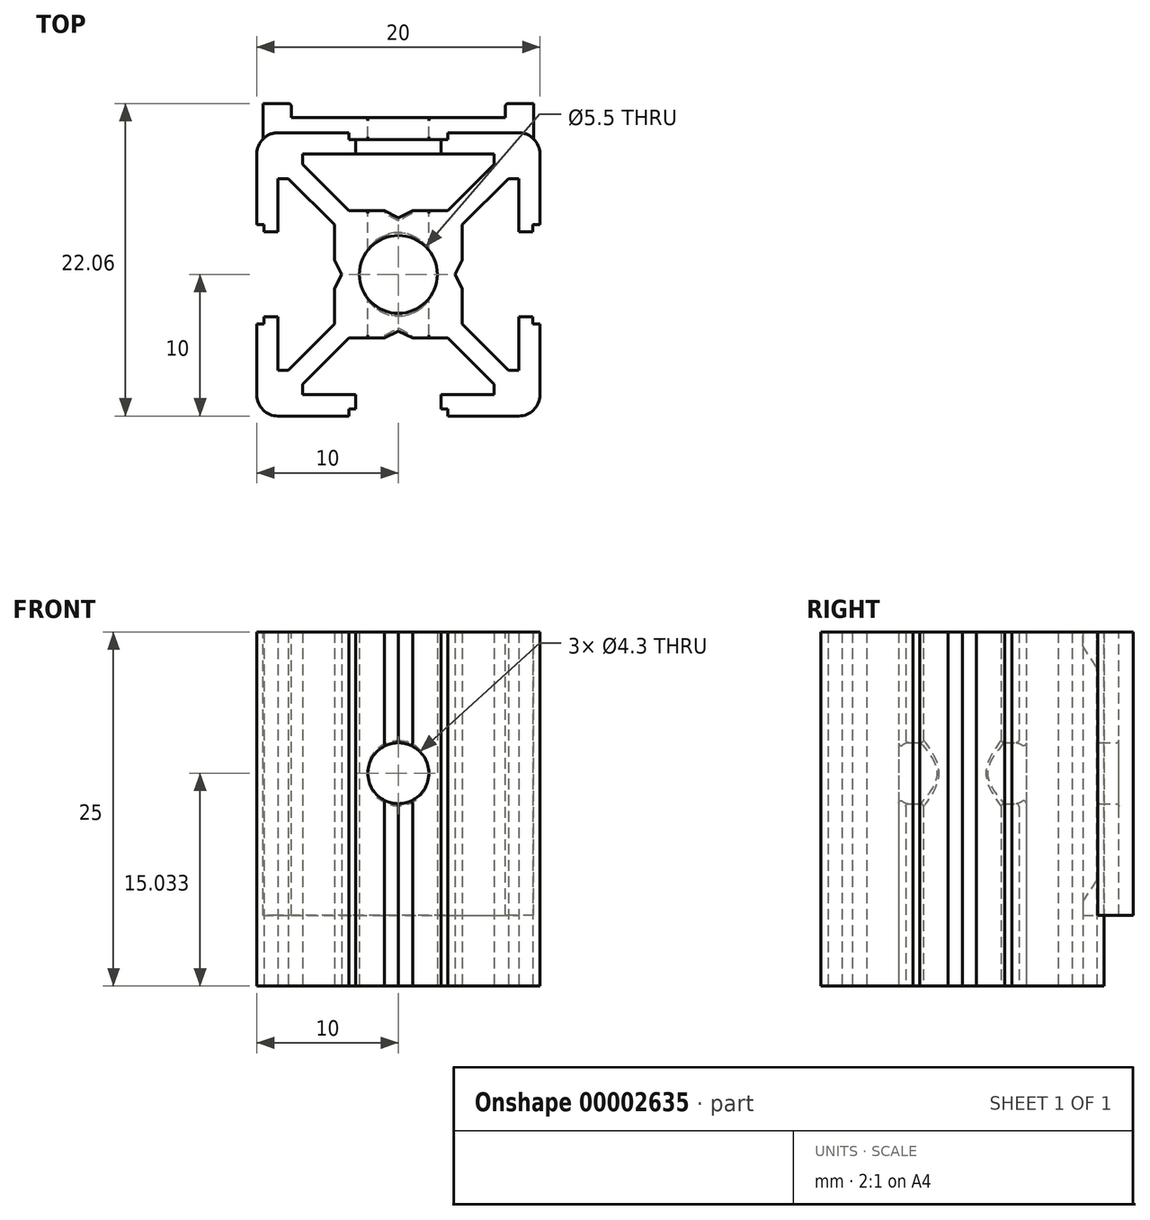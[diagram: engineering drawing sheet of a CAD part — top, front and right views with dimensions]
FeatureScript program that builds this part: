
annotation { "Feature Type Name" : "Feature", "Feature Type Description" : "" }
export const myFeature = defineFeature(function(context is Context, id is Id, definition is map)
    precondition{}
    {
        {
            var Q0;
            Q0=qCreatedBy(makeId("Top.planeOp"),FACE);
            var sketch = newSketch(context, id + "F0", { "sketchPlane" : qUnion([Q0])});
            skLineSegment(sketch, "E0", {"start": v(-1, -4.5) * mm, "end": v(-3.5, -4.5) * mm});
            skLineSegment(sketch, "E1", {"start": v(-6.77, -7.77) * mm, "end": v(-6.77, -8.5) * mm});
            skLineSegment(sketch, "E2", {"start": v(-6.77, -8.5) * mm, "end": v(-3, -8.5) * mm});
            skLineSegment(sketch, "E3", {"start": v(-3, -8.5) * mm, "end": v(-3, -9.5) * mm});
            skLineSegment(sketch, "E4", {"start": v(-5.56, -10) * mm, "end": v(-8.5, -10) * mm});
            skLineSegment(sketch, "E5", {"start": v(-1, -4.5) * mm, "end": v(0, -4) * mm});
            skLineSegment(sketch, "E6", {"start": v(-3, -9.5) * mm, "end": v(-3.5, -9.5) * mm});
            skLineSegment(sketch, "E7", {"start": v(-3.5, -9.5) * mm, "end": v(-3.5, -10) * mm, "construction": true});
            skArc(sketch, "E8.filletArc", {"start": v(-9.56, -9.56) * mm, "mid": v(-9.07, -9.89) * mm, "end": v(-8.5, -10) * mm});
            skLineSegment(sketch, "E9", {"start": v(-3.5, -10) * mm, "end": v(-5.56, -10) * mm});
            skPoint(sketch, "E10.orphan", {"position": v(0, -10) * mm});
            skLineSegment(sketch, "E11.trimOffspring", {"start": v(-8.5, -8.5) * mm, "end": v(-1.94, -1.94) * mm});
            skPoint(sketch, "E12", {"position": v(0, -4.5) * mm});
            skLineSegment(sketch, "E13", {"start": v(-3.5, -4.5) * mm, "end": v(-6.77, -7.77) * mm});
            skArc(sketch, "E14", {"start": v(-1.94, -1.94) * mm, "mid": v(-1.05, -2.54) * mm, "end": v(0, -2.75) * mm});
            skPoint(sketch, "E15", {"position": v(-1.94, -1.94) * mm});
            skLineSegment(sketch, "E16", {"start": v(0, -4) * mm, "end": v(0, -2.75) * mm});
            skLineSegment(sketch, "E17", {"start": v(-9.56, -9.56) * mm, "end": v(-8.5, -8.5) * mm});
            skPoint(sketch, "E18", {"position": v(-5.56, -10) * mm});
            skLineSegment(sketch, "E19", {"start": v(-3.5, -9.5) * mm, "end": v(-3.5, -10) * mm});
            skPoint(sketch, "E20.0.MirrorP", {"position": v(-10, -5.56) * mm});
            skPoint(sketch, "E20.1.MirrorP", {"position": v(-10, -5.56) * mm});
            skPoint(sketch, "E20.2.MirrorP", {"position": v(-10, -5.56) * mm});
            skPoint(sketch, "E20.3.MirrorP", {"position": v(-10, -5.56) * mm});
            skPoint(sketch, "E20.4.MirrorP", {"position": v(-10, -5.56) * mm});
            skPoint(sketch, "E20.5.MirrorP", {"position": v(-10, -5.56) * mm});
            skPoint(sketch, "E20.6.MirrorP", {"position": v(-10, -5.56) * mm});
            skPoint(sketch, "E20.7.MirrorP", {"position": v(-10, -5.56) * mm});
            skPoint(sketch, "E20.8.MirrorP", {"position": v(-10, -5.56) * mm});
            skPoint(sketch, "E20.9.MirrorP", {"position": v(-10, -5.56) * mm});
            skPoint(sketch, "E20.10.MirrorP", {"position": v(-10, -5.56) * mm});
            skLineSegment(sketch, "E20.11.MirrorCS", {"start": v(-9.5, -3.5) * mm, "end": v(-10, -3.5) * mm, "construction": true});
            skPoint(sketch, "E20.12.MirrorP", {"position": v(-10, -5.56) * mm});
            skLineSegment(sketch, "E20.13.MirrorCS", {"start": v(-9.5, -3.5) * mm, "end": v(-10, -3.5) * mm});
            skLineSegment(sketch, "E20.14.MirrorCS", {"start": v(-7.77, -6.77) * mm, "end": v(-8.5, -6.77) * mm});
            skPoint(sketch, "E20.15.MirrorP", {"position": v(-10, -5.56) * mm});
            skLineSegment(sketch, "E20.16.MirrorCS", {"start": v(-9.5, -3) * mm, "end": v(-9.5, -3.5) * mm});
            skPoint(sketch, "E20.17.MirrorP", {"position": v(-10, 0) * mm});
            skLineSegment(sketch, "E20.18.MirrorCS", {"start": v(-10, -5.56) * mm, "end": v(-10, -8.5) * mm});
            skArc(sketch, "E20.19.MirrorCS", {"start": v(-1.94, -1.94) * mm, "mid": v(-2.54, -1.05) * mm, "end": v(-2.75, 0) * mm});
            skPoint(sketch, "E20.20.MirrorP", {"position": v(-4.5, 0) * mm});
            skLineSegment(sketch, "E20.21.MirrorCS", {"start": v(-4.5, -3.5) * mm, "end": v(-7.77, -6.77) * mm});
            skLineSegment(sketch, "E20.23.MirrorCS", {"start": v(-4.5, -1) * mm, "end": v(-4.5, -3.5) * mm});
            skLineSegment(sketch, "E20.24.MirrorCS", {"start": v(-8.5, -6.77) * mm, "end": v(-8.5, -3) * mm});
            skLineSegment(sketch, "E20.25.MirrorCS", {"start": v(-10, -3.5) * mm, "end": v(-10, -5.56) * mm});
            skLineSegment(sketch, "E20.26.MirrorCS", {"start": v(-4, 0) * mm, "end": v(-2.75, 0) * mm});
            skArc(sketch, "E20.28.MirrorCS", {"start": v(-9.56, -9.56) * mm, "mid": v(-9.89, -9.07) * mm, "end": v(-10, -8.5) * mm});
            skLineSegment(sketch, "E20.29.MirrorCS", {"start": v(-4.5, -1) * mm, "end": v(-4, 0) * mm});
            skLineSegment(sketch, "E20.30.MirrorCS", {"start": v(-10, -5.56) * mm, "end": v(-10, -8.5) * mm});
            skPoint(sketch, "E20.31.MirrorP", {"position": v(-10, -5.56) * mm});
            skLineSegment(sketch, "E20.32.MirrorCS", {"start": v(-8.5, -3) * mm, "end": v(-9.5, -3) * mm});
            skPoint(sketch, "E21.0.MirrorP", {"position": v(-5.56, 10) * mm});
            skPoint(sketch, "E21.1.MirrorP", {"position": v(-10, 5.56) * mm});
            skPoint(sketch, "E21.2.MirrorP", {"position": v(-5.56, 10) * mm});
            skPoint(sketch, "E21.3.MirrorP", {"position": v(-10, 5.56) * mm});
            skPoint(sketch, "E21.4.MirrorP", {"position": v(-5.56, 10) * mm});
            skPoint(sketch, "E21.5.MirrorP", {"position": v(-10, 5.56) * mm});
            skPoint(sketch, "E21.6.MirrorP", {"position": v(-10, 5.56) * mm});
            skPoint(sketch, "E21.7.MirrorP", {"position": v(-5.56, 10) * mm});
            skPoint(sketch, "E21.8.MirrorP", {"position": v(-5.56, 10) * mm});
            skPoint(sketch, "E21.9.MirrorP", {"position": v(-10, 5.56) * mm});
            skPoint(sketch, "E21.10.MirrorP", {"position": v(-5.56, 10) * mm});
            skPoint(sketch, "E21.11.MirrorP", {"position": v(-10, 5.56) * mm});
            skPoint(sketch, "E21.12.MirrorP", {"position": v(-5.56, 10) * mm});
            skPoint(sketch, "E21.13.MirrorP", {"position": v(-10, 5.56) * mm});
            skPoint(sketch, "E21.14.MirrorP", {"position": v(-5.56, 10) * mm});
            skPoint(sketch, "E21.15.MirrorP", {"position": v(-10, 5.56) * mm});
            skPoint(sketch, "E21.16.MirrorP", {"position": v(-5.56, 10) * mm});
            skPoint(sketch, "E21.17.MirrorP", {"position": v(-10, 5.56) * mm});
            skLineSegment(sketch, "E21.18.MirrorCS", {"start": v(-9.5, 3.5) * mm, "end": v(-10, 3.5) * mm, "construction": true});
            skPoint(sketch, "E21.19.MirrorP", {"position": v(-5.56, 10) * mm});
            skPoint(sketch, "E21.20.MirrorP", {"position": v(-10, 5.56) * mm});
            skLineSegment(sketch, "E21.21.MirrorCS", {"start": v(-3.5, 9.5) * mm, "end": v(-3.5, 10) * mm, "construction": true});
            skLineSegment(sketch, "E21.22.MirrorCS", {"start": v(-3.5, 9.5) * mm, "end": v(-3.5, 10) * mm});
            skPoint(sketch, "E21.23.MirrorP", {"position": v(-5.56, 10) * mm});
            skLineSegment(sketch, "E21.24.MirrorCS", {"start": v(-9.5, 3.5) * mm, "end": v(-10, 3.5) * mm});
            skPoint(sketch, "E21.25.MirrorP", {"position": v(-10, 5.56) * mm});
            skPoint(sketch, "E21.26.MirrorP", {"position": v(-5.56, 10) * mm});
            skPoint(sketch, "E21.27.MirrorP", {"position": v(-10, 5.56) * mm});
            skLineSegment(sketch, "E21.28.MirrorCS", {"start": v(-3, 9.5) * mm, "end": v(-3.5, 9.5) * mm});
            skLineSegment(sketch, "E21.29.MirrorCS", {"start": v(-9.5, 3) * mm, "end": v(-9.5, 3.5) * mm});
            skLineSegment(sketch, "E21.30.MirrorCS", {"start": v(-8.5, 3) * mm, "end": v(-9.5, 3) * mm});
            skPoint(sketch, "E21.31.MirrorP", {"position": v(-5.56, 10) * mm});
            skPoint(sketch, "E21.32.MirrorP", {"position": v(-10, 5.56) * mm});
            skLineSegment(sketch, "E21.34.MirrorCS", {"start": v(-10, 3.5) * mm, "end": v(-10, 5.56) * mm});
            skArc(sketch, "E21.35.MirrorCS", {"start": v(-9.56, 9.56) * mm, "mid": v(-9.89, 9.07) * mm, "end": v(-10, 8.5) * mm});
            skLineSegment(sketch, "E21.36.MirrorCS", {"start": v(-8.5, 6.77) * mm, "end": v(-8.5, 3) * mm});
            skLineSegment(sketch, "E21.37.MirrorCS", {"start": v(-4.5, 1) * mm, "end": v(-4, 0) * mm});
            skLineSegment(sketch, "E21.38.MirrorCS", {"start": v(-10, 5.56) * mm, "end": v(-10, 8.5) * mm});
            skLineSegment(sketch, "E21.40.MirrorCS", {"start": v(-4.5, 3.5) * mm, "end": v(-7.77, 6.77) * mm});
            skLineSegment(sketch, "E21.41.MirrorCS", {"start": v(-4.5, 1) * mm, "end": v(-4.5, 3.5) * mm});
            skLineSegment(sketch, "E21.42.MirrorCS", {"start": v(-1, 4.5) * mm, "end": v(-3.5, 4.5) * mm});
            skLineSegment(sketch, "E21.43.MirrorCS", {"start": v(-6.77, 8.5) * mm, "end": v(-3, 8.5) * mm});
            skLineSegment(sketch, "E21.44.MirrorCS", {"start": v(-6.77, 7.77) * mm, "end": v(-6.77, 8.5) * mm});
            skLineSegment(sketch, "E21.45.MirrorCS", {"start": v(-5.56, 10) * mm, "end": v(-8.5, 10) * mm});
            skLineSegment(sketch, "E21.46.MirrorCS", {"start": v(-3, 8.5) * mm, "end": v(-3, 9.5) * mm});
            skLineSegment(sketch, "E21.47.MirrorCS", {"start": v(-1, 4.5) * mm, "end": v(0, 4) * mm});
            skLineSegment(sketch, "E21.48.MirrorCS", {"start": v(-5.56, 10) * mm, "end": v(-8.5, 10) * mm});
            skLineSegment(sketch, "E21.49.MirrorCS", {"start": v(-3.5, 10) * mm, "end": v(-5.56, 10) * mm});
            skArc(sketch, "E21.50.MirrorCS", {"start": v(-9.56, 9.56) * mm, "mid": v(-9.07, 9.89) * mm, "end": v(-8.5, 10) * mm});
            skLineSegment(sketch, "E21.51.MirrorCS", {"start": v(-3.5, 4.5) * mm, "end": v(-6.77, 7.77) * mm});
            skLineSegment(sketch, "E21.52.MirrorCS", {"start": v(-8.5, 8.5) * mm, "end": v(-1.94, 1.94) * mm});
            skLineSegment(sketch, "E21.53.MirrorCS", {"start": v(-9.56, 9.56) * mm, "end": v(-8.5, 8.5) * mm});
            skLineSegment(sketch, "E21.54.MirrorCS", {"start": v(-9.56, 9.56) * mm, "end": v(-8.5, 8.5) * mm});
            skLineSegment(sketch, "E21.55.MirrorCS", {"start": v(0, 4) * mm, "end": v(0, 2.75) * mm});
            skArc(sketch, "E21.56.MirrorCS", {"start": v(-1.94, 1.94) * mm, "mid": v(-1.05, 2.54) * mm, "end": v(0, 2.75) * mm});
            skPoint(sketch, "E21.58.MirrorP", {"position": v(0, 4.5) * mm});
            skLineSegment(sketch, "E21.59.MirrorCS", {"start": v(-7.77, 6.77) * mm, "end": v(-8.5, 6.77) * mm});
            skPoint(sketch, "E21.60.MirrorP", {"position": v(-5.56, 10) * mm});
            skArc(sketch, "E21.61.MirrorCS", {"start": v(-1.94, 1.94) * mm, "mid": v(-2.54, 1.05) * mm, "end": v(-2.75, 0) * mm});
            skPoint(sketch, "E21.62.MirrorP", {"position": v(0, 10) * mm});
            skPoint(sketch, "E21.63.MirrorP", {"position": v(-1.94, 1.94) * mm});
            skPoint(sketch, "E21.64.MirrorP", {"position": v(-1.94, 1.94) * mm});
            skLineSegment(sketch, "E21.65.MirrorCS", {"start": v(-10, 5.56) * mm, "end": v(-10, 8.5) * mm});
            skPoint(sketch, "E21.66.MirrorP", {"position": v(-10, 5.56) * mm});
            skPoint(sketch, "E22.0.MirrorP", {"position": v(10, 5.56) * mm});
            skPoint(sketch, "E22.1.MirrorP", {"position": v(5.56, -10) * mm});
            skPoint(sketch, "E22.2.MirrorP", {"position": v(5.56, 10) * mm});
            skPoint(sketch, "E22.3.MirrorP", {"position": v(10, 5.56) * mm});
            skPoint(sketch, "E22.4.MirrorP", {"position": v(10, -5.56) * mm});
            skPoint(sketch, "E22.5.MirrorP", {"position": v(5.56, -10) * mm});
            skPoint(sketch, "E22.6.MirrorP", {"position": v(5.56, -10) * mm});
            skPoint(sketch, "E22.7.MirrorP", {"position": v(10, 5.56) * mm});
            skPoint(sketch, "E22.8.MirrorP", {"position": v(5.56, 10) * mm});
            skPoint(sketch, "E22.9.MirrorP", {"position": v(10, -5.56) * mm});
            skPoint(sketch, "E22.10.MirrorP", {"position": v(10, 5.56) * mm});
            skPoint(sketch, "E22.11.MirrorP", {"position": v(5.56, -10) * mm});
            skPoint(sketch, "E22.12.MirrorP", {"position": v(5.56, 10) * mm});
            skPoint(sketch, "E22.13.MirrorP", {"position": v(10, -5.56) * mm});
            skPoint(sketch, "E22.14.MirrorP", {"position": v(10, 5.56) * mm});
            skPoint(sketch, "E22.15.MirrorP", {"position": v(5.56, -10) * mm});
            skPoint(sketch, "E22.16.MirrorP", {"position": v(10, -5.56) * mm});
            skPoint(sketch, "E22.17.MirrorP", {"position": v(5.56, 10) * mm});
            skPoint(sketch, "E22.18.MirrorP", {"position": v(5.56, -10) * mm});
            skPoint(sketch, "E22.19.MirrorP", {"position": v(5.56, 10) * mm});
            skPoint(sketch, "E22.20.MirrorP", {"position": v(10, 5.56) * mm});
            skPoint(sketch, "E22.21.MirrorP", {"position": v(10, -5.56) * mm});
            skPoint(sketch, "E22.22.MirrorP", {"position": v(10, -5.56) * mm});
            skPoint(sketch, "E22.23.MirrorP", {"position": v(5.56, -10) * mm});
            skPoint(sketch, "E22.24.MirrorP", {"position": v(10, 5.56) * mm});
            skPoint(sketch, "E22.25.MirrorP", {"position": v(5.56, 10) * mm});
            skPoint(sketch, "E22.26.MirrorP", {"position": v(10, -5.56) * mm});
            skPoint(sketch, "E22.27.MirrorP", {"position": v(10, 5.56) * mm});
            skPoint(sketch, "E22.28.MirrorP", {"position": v(5.56, -10) * mm});
            skPoint(sketch, "E22.29.MirrorP", {"position": v(5.56, 10) * mm});
            skPoint(sketch, "E22.30.MirrorP", {"position": v(10, -5.56) * mm});
            skPoint(sketch, "E22.31.MirrorP", {"position": v(5.56, 10) * mm});
            skPoint(sketch, "E22.32.MirrorP", {"position": v(5.56, -10) * mm});
            skPoint(sketch, "E22.33.MirrorP", {"position": v(10, 5.56) * mm});
            skPoint(sketch, "E22.34.MirrorP", {"position": v(10, 5.56) * mm});
            skPoint(sketch, "E22.35.MirrorP", {"position": v(5.56, 10) * mm});
            skPoint(sketch, "E22.36.MirrorP", {"position": v(10, -5.56) * mm});
            skPoint(sketch, "E22.37.MirrorP", {"position": v(5.56, -10) * mm});
            skLineSegment(sketch, "E22.38.MirrorCS", {"start": v(3.5, 9.5) * mm, "end": v(3.5, 10) * mm, "construction": true});
            skLineSegment(sketch, "E22.39.MirrorCS", {"start": v(9.5, 3.5) * mm, "end": v(10, 3.5) * mm, "construction": true});
            skLineSegment(sketch, "E22.40.MirrorCS", {"start": v(9.5, -3.5) * mm, "end": v(10, -3.5) * mm, "construction": true});
            skLineSegment(sketch, "E22.41.MirrorCS", {"start": v(3.5, -9.5) * mm, "end": v(3.5, -10) * mm, "construction": true});
            skPoint(sketch, "E22.42.MirrorP", {"position": v(10, 5.56) * mm});
            skPoint(sketch, "E22.43.MirrorP", {"position": v(10, -5.56) * mm});
            skPoint(sketch, "E22.44.MirrorP", {"position": v(5.56, -10) * mm});
            skPoint(sketch, "E22.45.MirrorP", {"position": v(5.56, 10) * mm});
            skLineSegment(sketch, "E22.46.MirrorCS", {"start": v(9.5, 3.5) * mm, "end": v(10, 3.5) * mm});
            skLineSegment(sketch, "E22.47.MirrorCS", {"start": v(9.5, -3) * mm, "end": v(9.5, -3.5) * mm});
            skLineSegment(sketch, "E22.48.MirrorCS", {"start": v(9.5, -3.5) * mm, "end": v(10, -3.5) * mm});
            skLineSegment(sketch, "E22.49.MirrorCS", {"start": v(9.56, -9.56) * mm, "end": v(8.5, -8.5) * mm});
            skLineSegment(sketch, "E22.50.MirrorCS", {"start": v(3, -9.5) * mm, "end": v(3.5, -9.5) * mm});
            skPoint(sketch, "E22.51.MirrorP", {"position": v(10, -5.56) * mm});
            skPoint(sketch, "E22.52.MirrorP", {"position": v(10, 5.56) * mm});
            skPoint(sketch, "E22.53.MirrorP", {"position": v(5.56, 10) * mm});
            skPoint(sketch, "E22.54.MirrorP", {"position": v(5.56, -10) * mm});
            skLineSegment(sketch, "E22.55.MirrorCS", {"start": v(3, 9.5) * mm, "end": v(3.5, 9.5) * mm});
            skLineSegment(sketch, "E22.56.MirrorCS", {"start": v(9.5, 3) * mm, "end": v(9.5, 3.5) * mm});
            skLineSegment(sketch, "E22.57.MirrorCS", {"start": v(3.5, -9.5) * mm, "end": v(3.5, -10) * mm});
            skLineSegment(sketch, "E22.58.MirrorCS", {"start": v(3.5, 9.5) * mm, "end": v(3.5, 10) * mm});
            skLineSegment(sketch, "E22.59.MirrorCS", {"start": v(3, 8.5) * mm, "end": v(3, 9.5) * mm});
            skLineSegment(sketch, "E22.60.MirrorCS", {"start": v(6.77, 7.77) * mm, "end": v(6.77, 8.5) * mm});
            skPoint(sketch, "E22.61.MirrorP", {"position": v(5.56, 10) * mm});
            skLineSegment(sketch, "E22.62.MirrorCS", {"start": v(6.77, -7.77) * mm, "end": v(6.77, -8.5) * mm});
            skPoint(sketch, "E22.63.MirrorP", {"position": v(5.56, -10) * mm});
            skPoint(sketch, "E22.64.MirrorP", {"position": v(10, -5.56) * mm});
            skLineSegment(sketch, "E22.65.MirrorCS", {"start": v(9.56, -9.56) * mm, "end": v(8.5, -8.5) * mm});
            skLineSegment(sketch, "E22.66.MirrorCS", {"start": v(7.77, 6.77) * mm, "end": v(8.5, 6.77) * mm});
            skLineSegment(sketch, "E22.67.MirrorCS", {"start": v(1, 4.5) * mm, "end": v(0, 4) * mm});
            skLineSegment(sketch, "E22.68.MirrorCS", {"start": v(4.5, -1) * mm, "end": v(4, 0) * mm});
            skLineSegment(sketch, "E22.69.MirrorCS", {"start": v(4, 0) * mm, "end": v(2.75, 0) * mm});
            skLineSegment(sketch, "E22.70.MirrorCS", {"start": v(1, -4.5) * mm, "end": v(0, -4) * mm});
            skLineSegment(sketch, "E22.71.MirrorCS", {"start": v(10, 5.56) * mm, "end": v(10, 8.5) * mm});
            skPoint(sketch, "E22.72.MirrorP", {"position": v(10, 5.56) * mm});
            skPoint(sketch, "E22.73.MirrorP", {"position": v(10, 0) * mm});
            skLineSegment(sketch, "E22.74.MirrorCS", {"start": v(9.56, 9.56) * mm, "end": v(8.5, 8.5) * mm});
            skLineSegment(sketch, "E22.75.MirrorCS", {"start": v(4.5, 1) * mm, "end": v(4, 0) * mm});
            skLineSegment(sketch, "E22.76.MirrorCS", {"start": v(7.77, -6.77) * mm, "end": v(8.5, -6.77) * mm});
            skLineSegment(sketch, "E22.78.MirrorCS", {"start": v(10, 5.56) * mm, "end": v(10, 8.5) * mm});
            skLineSegment(sketch, "E22.79.MirrorCS", {"start": v(3.5, -10) * mm, "end": v(5.56, -10) * mm});
            skLineSegment(sketch, "E22.80.MirrorCS", {"start": v(3, -8.5) * mm, "end": v(3, -9.5) * mm});
            skLineSegment(sketch, "E22.81.MirrorCS", {"start": v(5.56, -10) * mm, "end": v(8.5, -10) * mm});
            skPoint(sketch, "E22.83.MirrorP", {"position": v(5.56, -10) * mm});
            skLineSegment(sketch, "E22.84.MirrorCS", {"start": v(8.5, 3) * mm, "end": v(9.5, 3) * mm});
            skLineSegment(sketch, "E22.85.MirrorCS", {"start": v(3.5, 10) * mm, "end": v(5.56, 10) * mm});
            skArc(sketch, "E22.86.MirrorCS", {"start": v(1.94, -1.94) * mm, "mid": v(1.05, -2.54) * mm, "end": v(0, -2.75) * mm});
            skPoint(sketch, "E22.87.MirrorP", {"position": v(1.94, -1.94) * mm});
            skPoint(sketch, "E22.88.MirrorP", {"position": v(4.5, 0) * mm});
            skArc(sketch, "E22.89.MirrorCS", {"start": v(9.56, 9.56) * mm, "mid": v(9.07, 9.89) * mm, "end": v(8.5, 10) * mm});
            skLineSegment(sketch, "E22.90.MirrorCS", {"start": v(10, 3.5) * mm, "end": v(10, 5.56) * mm});
            skLineSegment(sketch, "E22.91.MirrorCS", {"start": v(8.5, -8.5) * mm, "end": v(1.94, -1.94) * mm});
            skLineSegment(sketch, "E22.92.MirrorCS", {"start": v(3.5, -4.5) * mm, "end": v(6.77, -7.77) * mm});
            skArc(sketch, "E22.93.MirrorCS", {"start": v(9.56, -9.56) * mm, "mid": v(9.07, -9.89) * mm, "end": v(8.5, -10) * mm});
            skLineSegment(sketch, "E22.94.MirrorCS", {"start": v(6.77, 8.5) * mm, "end": v(3, 8.5) * mm});
            skLineSegment(sketch, "E22.95.MirrorCS", {"start": v(4.5, 1) * mm, "end": v(4.5, 3.5) * mm});
            skLineSegment(sketch, "E22.96.MirrorCS", {"start": v(10, -5.56) * mm, "end": v(10, -8.5) * mm});
            skLineSegment(sketch, "E22.97.MirrorCS", {"start": v(5.56, -10) * mm, "end": v(8.5, -10) * mm});
            skPoint(sketch, "E22.99.MirrorP", {"position": v(5.56, 10) * mm});
            skLineSegment(sketch, "E22.101.MirrorCS", {"start": v(10, -5.56) * mm, "end": v(10, -8.5) * mm});
            skPoint(sketch, "E22.103.MirrorP", {"position": v(4.5, 0) * mm});
            skArc(sketch, "E22.104.MirrorCS", {"start": v(1.94, 1.94) * mm, "mid": v(1.05, 2.54) * mm, "end": v(0, 2.75) * mm});
            skArc(sketch, "E22.105.MirrorCS", {"start": v(1.94, -1.94) * mm, "mid": v(2.54, -1.05) * mm, "end": v(2.75, 0) * mm});
            skLineSegment(sketch, "E22.106.MirrorCS", {"start": v(4.5, 3.5) * mm, "end": v(7.77, 6.77) * mm});
            skLineSegment(sketch, "E22.107.MirrorCS", {"start": v(8.5, 8.5) * mm, "end": v(1.94, 1.94) * mm});
            skLineSegment(sketch, "E22.108.MirrorCS", {"start": v(8.5, -6.77) * mm, "end": v(8.5, -3) * mm});
            skArc(sketch, "E22.109.MirrorCS", {"start": v(9.56, -9.56) * mm, "mid": v(9.89, -9.07) * mm, "end": v(10, -8.5) * mm});
            skPoint(sketch, "E22.110.MirrorP", {"position": v(1.94, 1.94) * mm});
            skLineSegment(sketch, "E22.111.MirrorCS", {"start": v(6.77, -8.5) * mm, "end": v(3, -8.5) * mm});
            skLineSegment(sketch, "E22.112.MirrorCS", {"start": v(1, -4.5) * mm, "end": v(3.5, -4.5) * mm});
            skLineSegment(sketch, "E22.113.MirrorCS", {"start": v(4.5, -1) * mm, "end": v(4.5, -3.5) * mm});
            skLineSegment(sketch, "E22.114.MirrorCS", {"start": v(3.5, 4.5) * mm, "end": v(6.77, 7.77) * mm});
            skPoint(sketch, "E22.115.MirrorP", {"position": v(10, -5.56) * mm});
            skLineSegment(sketch, "E22.116.MirrorCS", {"start": v(9.56, 9.56) * mm, "end": v(8.5, 8.5) * mm});
            skLineSegment(sketch, "E22.117.MirrorCS", {"start": v(4, 0) * mm, "end": v(2.75, 0) * mm});
            skArc(sketch, "E22.118.MirrorCS", {"start": v(9.56, 9.56) * mm, "mid": v(9.89, 9.07) * mm, "end": v(10, 8.5) * mm});
            skPoint(sketch, "E22.119.MirrorP", {"position": v(5.56, 10) * mm});
            skLineSegment(sketch, "E22.120.MirrorCS", {"start": v(8.5, -3) * mm, "end": v(9.5, -3) * mm});
            skLineSegment(sketch, "E22.121.MirrorCS", {"start": v(1, 4.5) * mm, "end": v(3.5, 4.5) * mm});
            skArc(sketch, "E22.122.MirrorCS", {"start": v(1.94, 1.94) * mm, "mid": v(2.54, 1.05) * mm, "end": v(2.75, 0) * mm});
            skLineSegment(sketch, "E22.123.MirrorCS", {"start": v(5.56, 10) * mm, "end": v(8.5, 10) * mm});
            skPoint(sketch, "E22.124.MirrorP", {"position": v(10, 0) * mm});
            skLineSegment(sketch, "E22.125.MirrorCS", {"start": v(10, -3.5) * mm, "end": v(10, -5.56) * mm});
            skLineSegment(sketch, "E22.126.MirrorCS", {"start": v(5.56, 10) * mm, "end": v(8.5, 10) * mm});
            skLineSegment(sketch, "E22.127.MirrorCS", {"start": v(4.5, -3.5) * mm, "end": v(7.77, -6.77) * mm});
            skPoint(sketch, "E22.128.MirrorP", {"position": v(10, -5.56) * mm});
            skPoint(sketch, "E22.129.MirrorP", {"position": v(1.94, -1.94) * mm});
            skPoint(sketch, "E22.131.MirrorP", {"position": v(1.94, 1.94) * mm});
            skLineSegment(sketch, "E22.132.MirrorCS", {"start": v(8.5, 6.77) * mm, "end": v(8.5, 3) * mm});
            skPoint(sketch, "E22.133.MirrorP", {"position": v(10, 5.56) * mm});
            skSolve(sketch);
        }
        {
            var Q0;
            Q0=qSketchRegion(id+"F0",true);
            extrude(context, id + "F1", {"entities" : qUnion([Q0]), "depth" : 25 * mm});
        }
        {
            var Q0;
            Q0=makeQuery(id+"F1.opExtrude","CAP_FACE",FACE,{"disambiguationData":[OSD([sQuery(id+"F0.wireOp",EDGE,"E0"),sQuery(id+"F0.wireOp",EDGE,"E1"),sQuery(id+"F0.wireOp",EDGE,"E2"),sQuery(id+"F0.wireOp",EDGE,"E3"),sQuery(id+"F0.wireOp",EDGE,"E5"),sQuery(id+"F0.wireOp",EDGE,"E6"),sQuery(id+"F0.wireOp",EDGE,"E4"),sQuery(id+"F0.wireOp",EDGE,"E8.filletArc"),sQuery(id+"F0.wireOp",EDGE,"E13"),sQuery(id+"F0.wireOp",EDGE,"E14"),sQuery(id+"F0.wireOp",EDGE,"E19"),sQuery(id+"F0.wireOp",EDGE,"E20.13.MirrorCS"),sQuery(id+"F0.wireOp",EDGE,"E20.14.MirrorCS"),sQuery(id+"F0.wireOp",EDGE,"E20.16.MirrorCS"),sQuery(id+"F0.wireOp",EDGE,"E20.19.MirrorCS"),sQuery(id+"F0.wireOp",EDGE,"E20.21.MirrorCS"),sQuery(id+"F0.wireOp",EDGE,"E20.23.MirrorCS"),sQuery(id+"F0.wireOp",EDGE,"E20.24.MirrorCS"),sQuery(id+"F0.wireOp",EDGE,"E20.25.MirrorCS"),sQuery(id+"F0.wireOp",EDGE,"E20.28.MirrorCS"),sQuery(id+"F0.wireOp",EDGE,"E20.29.MirrorCS"),sQuery(id+"F0.wireOp",EDGE,"E20.32.MirrorCS"),sQuery(id+"F0.wireOp",EDGE,"E21.22.MirrorCS"),sQuery(id+"F0.wireOp",EDGE,"E21.24.MirrorCS"),sQuery(id+"F0.wireOp",EDGE,"E21.28.MirrorCS"),sQuery(id+"F0.wireOp",EDGE,"E21.29.MirrorCS"),sQuery(id+"F0.wireOp",EDGE,"E21.30.MirrorCS"),sQuery(id+"F0.wireOp",EDGE,"E21.35.MirrorCS"),sQuery(id+"F0.wireOp",EDGE,"E21.36.MirrorCS"),sQuery(id+"F0.wireOp",EDGE,"E21.37.MirrorCS"),sQuery(id+"F0.wireOp",EDGE,"E21.40.MirrorCS"),sQuery(id+"F0.wireOp",EDGE,"E21.41.MirrorCS"),sQuery(id+"F0.wireOp",EDGE,"E21.42.MirrorCS"),sQuery(id+"F0.wireOp",EDGE,"E21.43.MirrorCS"),sQuery(id+"F0.wireOp",EDGE,"E21.44.MirrorCS"),sQuery(id+"F0.wireOp",EDGE,"E21.46.MirrorCS"),sQuery(id+"F0.wireOp",EDGE,"E21.47.MirrorCS"),sQuery(id+"F0.wireOp",EDGE,"E21.49.MirrorCS"),sQuery(id+"F0.wireOp",EDGE,"E21.50.MirrorCS"),sQuery(id+"F0.wireOp",EDGE,"E21.51.MirrorCS"),sQuery(id+"F0.wireOp",EDGE,"E21.56.MirrorCS"),sQuery(id+"F0.wireOp",EDGE,"E21.59.MirrorCS"),sQuery(id+"F0.wireOp",EDGE,"E21.61.MirrorCS"),sQuery(id+"F0.wireOp",EDGE,"E21.65.MirrorCS"),sQuery(id+"F0.wireOp",EDGE,"E22.46.MirrorCS"),sQuery(id+"F0.wireOp",EDGE,"E22.47.MirrorCS"),sQuery(id+"F0.wireOp",EDGE,"E22.48.MirrorCS"),sQuery(id+"F0.wireOp",EDGE,"E22.50.MirrorCS"),sQuery(id+"F0.wireOp",EDGE,"E22.55.MirrorCS"),sQuery(id+"F0.wireOp",EDGE,"E22.56.MirrorCS"),sQuery(id+"F0.wireOp",EDGE,"E22.57.MirrorCS"),sQuery(id+"F0.wireOp",EDGE,"E22.58.MirrorCS"),sQuery(id+"F0.wireOp",EDGE,"E22.60.MirrorCS"),sQuery(id+"F0.wireOp",EDGE,"E22.80.MirrorCS"),sQuery(id+"F0.wireOp",EDGE,"E22.62.MirrorCS"),sQuery(id+"F0.wireOp",EDGE,"E22.66.MirrorCS"),sQuery(id+"F0.wireOp",EDGE,"E22.67.MirrorCS"),sQuery(id+"F0.wireOp",EDGE,"E22.68.MirrorCS"),sQuery(id+"F0.wireOp",EDGE,"E22.70.MirrorCS"),sQuery(id+"F0.wireOp",EDGE,"E22.75.MirrorCS"),sQuery(id+"F0.wireOp",EDGE,"E22.76.MirrorCS"),sQuery(id+"F0.wireOp",EDGE,"E22.59.MirrorCS"),sQuery(id+"F0.wireOp",EDGE,"E22.79.MirrorCS"),sQuery(id+"F0.wireOp",EDGE,"E22.84.MirrorCS"),sQuery(id+"F0.wireOp",EDGE,"E22.86.MirrorCS"),sQuery(id+"F0.wireOp",EDGE,"E22.89.MirrorCS"),sQuery(id+"F0.wireOp",EDGE,"E22.90.MirrorCS"),sQuery(id+"F0.wireOp",EDGE,"E22.92.MirrorCS"),sQuery(id+"F0.wireOp",EDGE,"E22.93.MirrorCS"),sQuery(id+"F0.wireOp",EDGE,"E22.94.MirrorCS"),sQuery(id+"F0.wireOp",EDGE,"E22.95.MirrorCS"),sQuery(id+"F0.wireOp",EDGE,"E22.96.MirrorCS"),sQuery(id+"F0.wireOp",EDGE,"E22.104.MirrorCS"),sQuery(id+"F0.wireOp",EDGE,"E22.105.MirrorCS"),sQuery(id+"F0.wireOp",EDGE,"E22.106.MirrorCS"),sQuery(id+"F0.wireOp",EDGE,"E22.108.MirrorCS"),sQuery(id+"F0.wireOp",EDGE,"E22.109.MirrorCS"),sQuery(id+"F0.wireOp",EDGE,"E22.111.MirrorCS"),sQuery(id+"F0.wireOp",EDGE,"E22.112.MirrorCS"),sQuery(id+"F0.wireOp",EDGE,"E22.113.MirrorCS"),sQuery(id+"F0.wireOp",EDGE,"E22.114.MirrorCS"),sQuery(id+"F0.wireOp",EDGE,"E22.118.MirrorCS"),sQuery(id+"F0.wireOp",EDGE,"E22.120.MirrorCS"),sQuery(id+"F0.wireOp",EDGE,"E22.121.MirrorCS"),sQuery(id+"F0.wireOp",EDGE,"E22.122.MirrorCS"),sQuery(id+"F0.wireOp",EDGE,"E22.123.MirrorCS"),sQuery(id+"F0.wireOp",EDGE,"E22.127.MirrorCS"),sQuery(id+"F0.wireOp",EDGE,"E22.132.MirrorCS")])],"isStart":false});
            var sketch = newSketch(context, id + "F2", { "sketchPlane" : qUnion([Q0])});
            skLineSegment(sketch, "E23", {"start": v(-3, 9.5) * mm, "end": v(3, 9.5) * mm});
            skPoint(sketch, "E24", {"position": v(-9.56, 9.56) * mm});
            skLineSegment(sketch, "E25", {"start": v(0, 0) * mm, "end": v(-9.56, 9.56) * mm, "construction": true});
            skLineSegment(sketch, "E26", {"start": v(-9.56, 9.56) * mm, "end": v(-14.07, 14.07) * mm, "construction": true});
            skLineSegment(sketch, "E27", {"start": v(-9.56, 9.56) * mm, "end": v(-9.56, 11.06) * mm});
            skLineSegment(sketch, "E28", {"start": v(-9.56, 11.06) * mm, "end": v(-11.06, 11.06) * mm});
            skLineSegment(sketch, "E29", {"start": v(-11.06, 11.06) * mm, "end": v(-9.56, 9.56) * mm});
            skLineSegment(sketch, "E30.0.MirrorCS", {"start": v(11.06, 11.06) * mm, "end": v(9.56, 9.56) * mm});
            skLineSegment(sketch, "E31.0.MirrorCS", {"start": v(9.56, 11.06) * mm, "end": v(11.06, 11.06) * mm});
            skLineSegment(sketch, "E32.0.MirrorCS", {"start": v(9.56, 9.56) * mm, "end": v(9.56, 11.06) * mm});
            skLineSegment(sketch, "E33", {"start": v(-9.56, 11.06) * mm, "end": v(9.56, 11.06) * mm});
            skLineSegment(sketch, "E34", {"start": v(-9.56, 11.06) * mm, "end": v(-9.56, 12.06) * mm});
            skLineSegment(sketch, "E35", {"start": v(-9.56, 12.06) * mm, "end": v(-7.56, 12.06) * mm});
            skLineSegment(sketch, "E36", {"start": v(-7.56, 12.06) * mm, "end": v(-7.56, 11.06) * mm});
            skLineSegment(sketch, "E37.0.MirrorCS", {"start": v(7.56, 12.06) * mm, "end": v(7.56, 11.06) * mm});
            skLineSegment(sketch, "E38.0.MirrorCS", {"start": v(9.56, 12.06) * mm, "end": v(7.56, 12.06) * mm});
            skLineSegment(sketch, "E39.0.MirrorCS", {"start": v(9.56, 11.06) * mm, "end": v(9.56, 12.06) * mm});
            skLineSegment(sketch, "E40", {"start": v(-3, 8.5) * mm, "end": v(3, 8.5) * mm});
            skSolve(sketch);
        }
        {
            var Q0;
            Q0=makeQuery(id+"F2.imprint","IMPRINT",FACE,{"disambiguationData":[TD([[makeQuery(id+"F2.imprint","IMPRINT",EDGE,{"derivedFrom":sQuery(id+"F2.wireOp",EDGE,"E23")}),1.0]])]});
            var Q1;
            {var subQ1=sQuery(id+"F2.wireOp",EDGE,"E34");Q1=makeQuery(id+"F2.imprint","IMPRINT",FACE,{"disambiguationData":[TD([[makeQuery(id+"F2.imprint","IMPRINT",EDGE,{"derivedFrom":subQ1}),-1.0]])]});}
            var Q2;
            {var subQ1=sQuery(id+"F2.wireOp",EDGE,"E37.0.MirrorCS");Q2=makeQuery(id+"F2.imprint","IMPRINT",FACE,{"disambiguationData":[TD([[makeQuery(id+"F2.imprint","IMPRINT",EDGE,{"derivedFrom":subQ1}),1.0]])]});}
            extrude(context, id + "F3", {"entities" : qUnion([Q0, Q1, Q2]), "oppositeDirection" : true, "depth" : 20 * mm});
        }
        {
            var Q0;
            Q0=makeQuery(id+"F3.opExtrude","SWEPT_EDGE",EDGE,{"disambiguationData":[OSD([sQuery(id+"F0.wireOp",EDGE,"E21.22.MirrorCS"),sQuery(id+"F0.wireOp",EDGE,"E21.28.MirrorCS")])]});
            var Q1;
            Q1=makeQuery(id+"F3.opExtrude","SWEPT_EDGE",EDGE,{"disambiguationData":[OSD([sQuery(id+"F0.wireOp",EDGE,"E22.55.MirrorCS"),sQuery(id+"F0.wireOp",EDGE,"E22.58.MirrorCS")])]});
            var Q2;
            Q2=makeQuery(id+"F3.opExtrude","SWEPT_EDGE",EDGE,{"disambiguationData":[OSD([sQuery(id+"F2.wireOp",EDGE,"E35"),sQuery(id+"F2.wireOp",EDGE,"E36")])]});
            var Q3;
            Q3=makeQuery(id+"F3.opExtrude","SWEPT_EDGE",EDGE,{"disambiguationData":[OSD([sQuery(id+"F2.wireOp",EDGE,"E37.0.MirrorCS"),sQuery(id+"F2.wireOp",EDGE,"E38.0.MirrorCS")])]});
            fillet(context, id + "F4", {"entities" : qUnion([Q0, Q1, Q2, Q3]), "radius" : 0.2 * mm, "tangentPropagation" : true, "allowEdgeOverflow" : false});
        }
        {
            var Q0;
            Q0=makeQuery(id+"F2.imprint","IMPRINT",FACE,{"disambiguationData":[TD([[makeQuery(id+"F2.imprint","IMPRINT",EDGE,{"derivedFrom":sQuery(id+"F2.wireOp",EDGE,"E23")}),-1.0]])]});
            extrude(context, id + "F5", {"entities" : qUnion([Q0]), "oppositeDirection" : true, "depth" : 2.5 * mm});
        }
        {
            var Q0;
            Q0=makeQuery(id+"F5.opExtrude","CAP_EDGE",EDGE,{"disambiguationData":[OSD([sQuery(id+"F2.wireOp",EDGE,"E40")])],"isStart":false});
            chamfer(context, id + "F6", {"entities" : qUnion([Q0]), "chamferType" : ChamferType.TWO_OFFSETS, "width1" : 1.5 * mm, "oppositeDirection" : false, "width2" : 1 * mm, "tangentPropagation" : true});
        }
        {
            var Q0;
            Q0=makeQuery(id+"F3.opExtrude","SWEPT_FACE",FACE,{"disambiguationData":[OSD([sQuery(id+"F0.wireOp",EDGE,"E21.49.MirrorCS")])]});
            var sketch = newSketch(context, id + "F7", { "sketchPlane" : qUnion([Q0])});
            skLineSegment(sketch, "E41", {"start": v(-8.5, 15) * mm, "end": v(7.97, 15) * mm, "construction": true});
            skSolve(sketch);
        }
        {
            var Q0;
            Q0=sQuery(id+"F7.wireOp",EDGE,"E41");
            cPlane(context, id + "F8", {"entities" : qUnion([Q0]), "cplaneType" : CPlaneType.LINE_ANGLE, "offset" : 150 * mm, "angle" : 90 * degree, "width" : 150 * mm, "height" : 150 * mm});
        }
        {
            var Q0;
            Q0=makeQuery(id+"F5.opExtrude","SWEPT_BODY",BODY,{"disambiguationData":[OSD([sQuery(id+"F0.wireOp",EDGE,"E21.46.MirrorCS"),sQuery(id+"F0.wireOp",EDGE,"E22.59.MirrorCS"),sQuery(id+"F2.wireOp",EDGE,"E23"),sQuery(id+"F2.wireOp",EDGE,"E40")])]});
            var Q1;
            Q1=qCreatedBy(id+"F8.planeOp",FACE);
            mirror(context, id + "F9", {"entities" : qUnion([Q0]), "mirrorPlane" : qUnion([Q1])});
        }
        {
            var Q0;
            Q0=makeQuery(id+"F3.opExtrude","SWEPT_FACE",FACE,{"disambiguationData":[OSD([sQuery(id+"F2.wireOp",EDGE,"E33")])]});
            var sketch = newSketch(context, id + "F10", { "sketchPlane" : qUnion([Q0])});
            skLineSegment(sketch, "E42", {"start": v(0, 5) * mm, "end": v(0, 23.33) * mm, "construction": true});
            skCircle(sketch, "E43", {"center": v(0, 15.03) * mm, "radius": 2.15 * mm});
            skSolve(sketch);
        }
        {
            var Q0;
            Q0=makeQuery(id+"F10.imprint","IMPRINT",FACE,{"disambiguationData":[TD([[makeQuery(id+"F10.imprint","IMPRINT",EDGE,{"derivedFrom":sQuery(id+"F10.wireOp",EDGE,"E43")}),1.0]])]});
            extrude(context, id + "F11", {"entities" : qUnion([Q0]), "operationType" : NewBodyOperationType.REMOVE, "oppositeDirection" : true, "depth" : 25 * mm});
        }
        {
            var Q0;
            Q0=makeQuery(id+"F11.boolean.opBoolean","COPY",FACE,{"derivedFrom":makeQuery(id+"F11.opExtrude","SWEPT_FACE",FACE,{"disambiguationData":[OSD([sQuery(id+"F10.wireOp",EDGE,"E43")])]})});
            fillet(context, id + "F12", {"entities" : qUnion([Q0]), "radius" : 0.2 * mm, "tangentPropagation" : true, "allowEdgeOverflow" : false});
        }
    });
